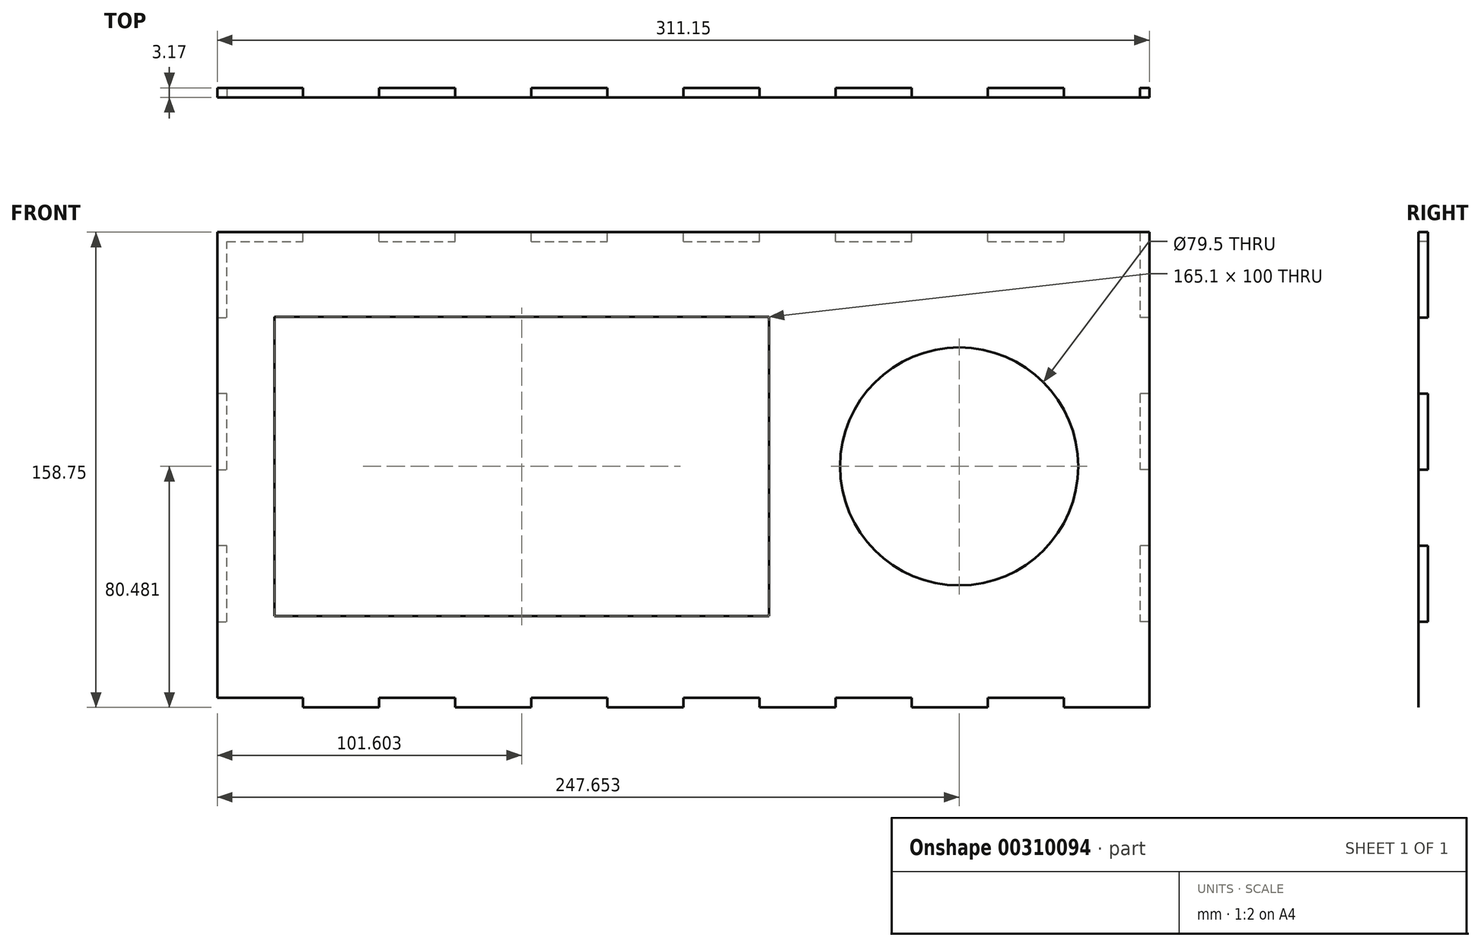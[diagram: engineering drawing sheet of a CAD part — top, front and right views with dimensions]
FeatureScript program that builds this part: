
annotation { "Feature Type Name" : "Feature", "Feature Type Description" : "" }
export const myFeature = defineFeature(function(context is Context, id is Id, definition is map)
    precondition{}
    {
        {
            var Q0;
            Q0=qCreatedBy(makeId("Front.planeOp"),FACE);
            var sketch = newSketch(context, id + "F0", { "sketchPlane" : qUnion([Q0])});
            skLineSegment(sketch, "E0.MirrorCS", {"start": v(-153.56, -44.26) * mm, "end": v(-153.56, -47.44) * mm});
            skLineSegment(sketch, "E1.MirrorCS", {"start": v(-128.16, -44.26) * mm, "end": v(-128.16, -47.44) * mm});
            skLineSegment(sketch, "E2.MirrorCS", {"start": v(-102.76, -44.26) * mm, "end": v(-102.76, -47.44) * mm});
            skLineSegment(sketch, "E3.MirrorCS", {"start": v(-77.36, -44.26) * mm, "end": v(-77.36, -47.44) * mm});
            skLineSegment(sketch, "E4.MirrorCS", {"start": v(-51.96, -44.26) * mm, "end": v(-51.96, -47.44) * mm});
            skLineSegment(sketch, "E5.MirrorCS", {"start": v(-1.16, -44.26) * mm, "end": v(-1.16, -47.44) * mm});
            skLineSegment(sketch, "E6.MirrorCS", {"start": v(-26.56, -44.26) * mm, "end": v(-26.56, -47.44) * mm});
            skLineSegment(sketch, "E7.MirrorCS", {"start": v(49.64, -44.26) * mm, "end": v(49.64, -47.44) * mm});
            skLineSegment(sketch, "E8.MirrorCS", {"start": v(24.24, -44.26) * mm, "end": v(24.24, -47.44) * mm});
            skLineSegment(sketch, "E9.MirrorCS", {"start": v(75.04, -44.26) * mm, "end": v(75.04, -47.44) * mm});
            skLineSegment(sketch, "E10", {"start": v(-178.96, -44.26) * mm, "end": v(-153.56, -44.26) * mm});
            skLineSegment(sketch, "E11", {"start": v(-128.16, -44.26) * mm, "end": v(-102.76, -44.26) * mm});
            skLineSegment(sketch, "E12", {"start": v(-102.76, -47.44) * mm, "end": v(-77.36, -47.44) * mm});
            skLineSegment(sketch, "E13", {"start": v(-77.36, -44.26) * mm, "end": v(-51.96, -44.26) * mm});
            skLineSegment(sketch, "E14", {"start": v(-51.96, -47.44) * mm, "end": v(-26.56, -47.44) * mm});
            skLineSegment(sketch, "E15", {"start": v(-26.56, -44.26) * mm, "end": v(-1.16, -44.26) * mm});
            skLineSegment(sketch, "E16", {"start": v(24.24, -44.26) * mm, "end": v(49.64, -44.26) * mm});
            skLineSegment(sketch, "E17", {"start": v(49.64, -47.44) * mm, "end": v(75.04, -47.44) * mm});
            skLineSegment(sketch, "E18", {"start": v(75.04, -44.26) * mm, "end": v(100.44, -44.26) * mm});
            skLineSegment(sketch, "E19", {"start": v(-182.14, -44.26) * mm, "end": v(-182.14, -18.86) * mm});
            skLineSegment(sketch, "E20", {"start": v(-182.14, -18.86) * mm, "end": v(-178.96, -18.86) * mm});
            skLineSegment(sketch, "E21", {"start": v(-178.96, -18.86) * mm, "end": v(-178.96, 6.54) * mm});
            skLineSegment(sketch, "E22", {"start": v(-178.96, 6.54) * mm, "end": v(-182.14, 6.54) * mm});
            skLineSegment(sketch, "E23", {"start": v(-182.14, 6.54) * mm, "end": v(-182.14, 31.94) * mm});
            skLineSegment(sketch, "E24", {"start": v(-182.14, 31.94) * mm, "end": v(-178.96, 31.94) * mm});
            skLineSegment(sketch, "E25", {"start": v(-178.96, 31.94) * mm, "end": v(-178.96, 57.34) * mm});
            skLineSegment(sketch, "E26", {"start": v(-178.96, 57.34) * mm, "end": v(-182.14, 57.34) * mm});
            skLineSegment(sketch, "E27", {"start": v(-182.14, 57.34) * mm, "end": v(-182.14, 82.74) * mm});
            skLineSegment(sketch, "E28", {"start": v(-182.14, 82.74) * mm, "end": v(-178.96, 82.74) * mm});
            skLineSegment(sketch, "E29", {"start": v(-178.96, 82.74) * mm, "end": v(-178.96, 108.14) * mm});
            skLineSegment(sketch, "E30", {"start": v(-178.96, 108.14) * mm, "end": v(-153.56, 108.14) * mm});
            skLineSegment(sketch, "E31", {"start": v(125.84, 108.14) * mm, "end": v(125.84, 82.74) * mm});
            skLineSegment(sketch, "E32", {"start": v(-1.16, -47.44) * mm, "end": v(24.24, -47.44) * mm});
            skLineSegment(sketch, "E33", {"start": v(-153.56, -47.44) * mm, "end": v(-128.16, -47.44) * mm});
            skLineSegment(sketch, "E34", {"start": v(125.84, -47.44) * mm, "end": v(100.44, -47.44) * mm});
            skLineSegment(sketch, "E35", {"start": v(100.44, -47.44) * mm, "end": v(100.44, -44.26) * mm});
            skLineSegment(sketch, "E36.MirrorCS", {"start": v(-153.56, 111.31) * mm, "end": v(-128.16, 111.31) * mm});
            skLineSegment(sketch, "E37.MirrorCS", {"start": v(-102.76, 111.31) * mm, "end": v(-77.36, 111.31) * mm});
            skLineSegment(sketch, "E38.MirrorCS", {"start": v(-51.96, 111.31) * mm, "end": v(-26.56, 111.31) * mm});
            skLineSegment(sketch, "E39.MirrorCS", {"start": v(-1.16, 111.31) * mm, "end": v(24.24, 111.31) * mm});
            skLineSegment(sketch, "E40.MirrorCS", {"start": v(49.64, 111.31) * mm, "end": v(75.04, 111.31) * mm});
            skLineSegment(sketch, "E41.MirrorCS", {"start": v(125.84, 111.31) * mm, "end": v(100.44, 111.31) * mm});
            skLineSegment(sketch, "E42.MirrorCS", {"start": v(-153.56, 108.14) * mm, "end": v(-153.56, 111.31) * mm});
            skLineSegment(sketch, "E43.MirrorCS", {"start": v(-128.16, 108.14) * mm, "end": v(-128.16, 111.31) * mm});
            skLineSegment(sketch, "E44.MirrorCS", {"start": v(-102.76, 108.14) * mm, "end": v(-102.76, 111.31) * mm});
            skLineSegment(sketch, "E45.MirrorCS", {"start": v(-51.96, 108.14) * mm, "end": v(-51.96, 111.31) * mm});
            skLineSegment(sketch, "E46.MirrorCS", {"start": v(-77.36, 108.14) * mm, "end": v(-77.36, 111.31) * mm});
            skLineSegment(sketch, "E47.MirrorCS", {"start": v(100.44, 111.31) * mm, "end": v(100.44, 108.14) * mm});
            skLineSegment(sketch, "E48.MirrorCS", {"start": v(75.04, 108.14) * mm, "end": v(75.04, 111.31) * mm});
            skLineSegment(sketch, "E49.MirrorCS", {"start": v(49.64, 108.14) * mm, "end": v(49.64, 111.31) * mm});
            skLineSegment(sketch, "E50.MirrorCS", {"start": v(24.24, 108.14) * mm, "end": v(24.24, 111.31) * mm});
            skLineSegment(sketch, "E51.MirrorCS", {"start": v(-26.56, 108.14) * mm, "end": v(-26.56, 111.31) * mm});
            skLineSegment(sketch, "E52.MirrorCS", {"start": v(-1.16, 108.14) * mm, "end": v(-1.16, 111.31) * mm});
            skLineSegment(sketch, "E53.trimOffspring", {"start": v(-128.16, 108.14) * mm, "end": v(-102.76, 108.14) * mm});
            skLineSegment(sketch, "E54.trimOffspring", {"start": v(-77.36, 108.14) * mm, "end": v(-51.96, 108.14) * mm});
            skLineSegment(sketch, "E55.trimOffspring", {"start": v(-26.56, 108.14) * mm, "end": v(-1.16, 108.14) * mm});
            skLineSegment(sketch, "E56.trimOffspring", {"start": v(24.24, 108.14) * mm, "end": v(49.64, 108.14) * mm});
            skLineSegment(sketch, "E57.trimOffspring", {"start": v(75.04, 108.14) * mm, "end": v(100.44, 108.14) * mm});
            skLineSegment(sketch, "E58.MirrorCS", {"start": v(129.01, 57.34) * mm, "end": v(129.01, 82.74) * mm});
            skLineSegment(sketch, "E59.MirrorCS", {"start": v(129.01, 6.54) * mm, "end": v(129.01, 31.94) * mm});
            skLineSegment(sketch, "E60.MirrorCS", {"start": v(129.01, -44.26) * mm, "end": v(129.01, -18.86) * mm});
            skLineSegment(sketch, "E61", {"start": v(129.01, -18.86) * mm, "end": v(125.84, -18.86) * mm});
            skLineSegment(sketch, "E62", {"start": v(129.01, 6.54) * mm, "end": v(125.84, 6.54) * mm});
            skLineSegment(sketch, "E63", {"start": v(129.01, 31.94) * mm, "end": v(125.84, 31.94) * mm});
            skLineSegment(sketch, "E64", {"start": v(125.84, 111.31) * mm, "end": v(125.84, 108.14) * mm});
            skLineSegment(sketch, "E65", {"start": v(129.01, 82.74) * mm, "end": v(125.84, 82.74) * mm});
            skLineSegment(sketch, "E66", {"start": v(129.01, 57.34) * mm, "end": v(125.84, 57.34) * mm});
            skLineSegment(sketch, "E67.trimOffspring", {"start": v(125.84, 57.34) * mm, "end": v(125.84, 31.94) * mm});
            skLineSegment(sketch, "E68.trimOffspring", {"start": v(125.84, 6.54) * mm, "end": v(125.84, -18.86) * mm});
            skLineSegment(sketch, "E69", {"start": v(125.84, -47.44) * mm, "end": v(129.01, -47.44) * mm});
            skLineSegment(sketch, "E70", {"start": v(129.01, -47.44) * mm, "end": v(129.01, -44.26) * mm});
            skPoint(sketch, "E71.end.orphan", {"position": v(125.84, -44.26) * mm});
            skLineSegment(sketch, "E72", {"start": v(-182.14, -44.26) * mm, "end": v(-178.96, -44.26) * mm});
            skPoint(sketch, "E73.end.orphan", {"position": v(-178.96, -47.44) * mm});
            skPoint(sketch, "E74.end.orphan", {"position": v(-182.14, -47.44) * mm});
            skSolve(sketch);
        }
        {
            var Q0;
            Q0=makeQuery(id+"F0.imprint","IMPRINT",FACE,{"disambiguationData":[TD([[makeQuery(id+"F0.imprint","IMPRINT",EDGE,{"derivedFrom":sQuery(id+"F0.wireOp",EDGE,"E0.MirrorCS")}),1.0]])]});
            var Q1;
            Q1=makeQuery(id+"F0.imprint","IMPRINT",FACE,{"disambiguationData":[TD([[makeQuery(id+"F0.imprint","IMPRINT",EDGE,{"derivedFrom":sQuery(id+"F0.wireOp",EDGE,"E5.MirrorCS")}),1.0]])]});
            extrude(context, id + "F1", {"entities" : qUnion([Q0, Q1]), "depth" : 1 / 203.2 * mm});
        }
        {
            var Q0;
            Q0=makeQuery(id+"F1.opExtrude","CAP_FACE",FACE,{"disambiguationData":[OSD([sQuery(id+"F0.wireOp",EDGE,"E0.MirrorCS"),sQuery(id+"F0.wireOp",EDGE,"E1.MirrorCS"),sQuery(id+"F0.wireOp",EDGE,"E2.MirrorCS"),sQuery(id+"F0.wireOp",EDGE,"E3.MirrorCS"),sQuery(id+"F0.wireOp",EDGE,"E4.MirrorCS"),sQuery(id+"F0.wireOp",EDGE,"E5.MirrorCS"),sQuery(id+"F0.wireOp",EDGE,"E6.MirrorCS"),sQuery(id+"F0.wireOp",EDGE,"E7.MirrorCS"),sQuery(id+"F0.wireOp",EDGE,"E8.MirrorCS"),sQuery(id+"F0.wireOp",EDGE,"E9.MirrorCS"),sQuery(id+"F0.wireOp",EDGE,"E10"),sQuery(id+"F0.wireOp",EDGE,"E11"),sQuery(id+"F0.wireOp",EDGE,"E12"),sQuery(id+"F0.wireOp",EDGE,"E13"),sQuery(id+"F0.wireOp",EDGE,"E14"),sQuery(id+"F0.wireOp",EDGE,"E15"),sQuery(id+"F0.wireOp",EDGE,"E16"),sQuery(id+"F0.wireOp",EDGE,"E17"),sQuery(id+"F0.wireOp",EDGE,"E18"),sQuery(id+"F0.wireOp",EDGE,"E19"),sQuery(id+"F0.wireOp",EDGE,"E20"),sQuery(id+"F0.wireOp",EDGE,"E21"),sQuery(id+"F0.wireOp",EDGE,"E22"),sQuery(id+"F0.wireOp",EDGE,"E23"),sQuery(id+"F0.wireOp",EDGE,"E24"),sQuery(id+"F0.wireOp",EDGE,"E25"),sQuery(id+"F0.wireOp",EDGE,"E26"),sQuery(id+"F0.wireOp",EDGE,"E27"),sQuery(id+"F0.wireOp",EDGE,"E28"),sQuery(id+"F0.wireOp",EDGE,"E29"),sQuery(id+"F0.wireOp",EDGE,"E30"),sQuery(id+"F0.wireOp",EDGE,"E31"),sQuery(id+"F0.wireOp",EDGE,"E32"),sQuery(id+"F0.wireOp",EDGE,"E33"),sQuery(id+"F0.wireOp",EDGE,"E34"),sQuery(id+"F0.wireOp",EDGE,"E35"),sQuery(id+"F0.wireOp",EDGE,"E36.MirrorCS"),sQuery(id+"F0.wireOp",EDGE,"E37.MirrorCS"),sQuery(id+"F0.wireOp",EDGE,"E38.MirrorCS"),sQuery(id+"F0.wireOp",EDGE,"E39.MirrorCS"),sQuery(id+"F0.wireOp",EDGE,"E40.MirrorCS"),sQuery(id+"F0.wireOp",EDGE,"E41.MirrorCS"),sQuery(id+"F0.wireOp",EDGE,"E42.MirrorCS"),sQuery(id+"F0.wireOp",EDGE,"E43.MirrorCS"),sQuery(id+"F0.wireOp",EDGE,"E44.MirrorCS"),sQuery(id+"F0.wireOp",EDGE,"E46.MirrorCS"),sQuery(id+"F0.wireOp",EDGE,"E47.MirrorCS"),sQuery(id+"F0.wireOp",EDGE,"E48.MirrorCS"),sQuery(id+"F0.wireOp",EDGE,"E49.MirrorCS"),sQuery(id+"F0.wireOp",EDGE,"E50.MirrorCS"),sQuery(id+"F0.wireOp",EDGE,"E45.MirrorCS"),sQuery(id+"F0.wireOp",EDGE,"E51.MirrorCS"),sQuery(id+"F0.wireOp",EDGE,"E52.MirrorCS"),sQuery(id+"F0.wireOp",EDGE,"E53.trimOffspring"),sQuery(id+"F0.wireOp",EDGE,"E54.trimOffspring"),sQuery(id+"F0.wireOp",EDGE,"E55.trimOffspring"),sQuery(id+"F0.wireOp",EDGE,"E56.trimOffspring"),sQuery(id+"F0.wireOp",EDGE,"E57.trimOffspring"),sQuery(id+"F0.wireOp",EDGE,"E58.MirrorCS"),sQuery(id+"F0.wireOp",EDGE,"E59.MirrorCS"),sQuery(id+"F0.wireOp",EDGE,"E60.MirrorCS"),sQuery(id+"F0.wireOp",EDGE,"E61"),sQuery(id+"F0.wireOp",EDGE,"E62"),sQuery(id+"F0.wireOp",EDGE,"E63"),sQuery(id+"F0.wireOp",EDGE,"E64"),sQuery(id+"F0.wireOp",EDGE,"E65"),sQuery(id+"F0.wireOp",EDGE,"E66"),sQuery(id+"F0.wireOp",EDGE,"E67.trimOffspring"),sQuery(id+"F0.wireOp",EDGE,"E68.trimOffspring"),sQuery(id+"F0.wireOp",EDGE,"E69"),sQuery(id+"F0.wireOp",EDGE,"E70"),sQuery(id+"F0.wireOp",EDGE,"E74"),sQuery(id+"F0.wireOp",EDGE,"E73"),sQuery(id+"F0.wireOp",EDGE,"YqXnORVU-T2M5-09My-Jtlm-RCLeSNGwjOX8")])],"isStart":false});
            var sketch = newSketch(context, id + "F2", { "sketchPlane" : qUnion([Q0])});
            skLineSegment(sketch, "E75.bottom", {"start": v(-163.09, 83.04) * mm, "end": v(2.01, 83.04) * mm});
            skLineSegment(sketch, "E75.top", {"start": v(-163.09, -16.96) * mm, "end": v(2.01, -16.96) * mm});
            skLineSegment(sketch, "E75.left", {"start": v(-163.09, 83.04) * mm, "end": v(-163.09, -16.96) * mm});
            skLineSegment(sketch, "E75.right", {"start": v(2.01, 83.04) * mm, "end": v(2.01, -16.96) * mm});
            skCircle(sketch, "E76", {"center": v(65.51, 33.04) * mm, "radius": 39.75 * mm});
            skPoint(sketch, "E76.centerSnap0", {"position": v(2.01, 33.04) * mm});
            skSolve(sketch);
        }
        {
            var Q0;
            Q0=makeQuery(id+"F2.imprint","IMPRINT",FACE,{"disambiguationData":[TD([[makeQuery(id+"F2.imprint","IMPRINT",EDGE,{"derivedFrom":sQuery(id+"F2.wireOp",EDGE,"E75.bottom")}),-1.0]])]});
            var Q1;
            Q1=makeQuery(id+"F2.imprint","IMPRINT",FACE,{"disambiguationData":[TD([[makeQuery(id+"F2.imprint","IMPRINT",EDGE,{"derivedFrom":sQuery(id+"F2.wireOp",EDGE,"E76")}),1.0]])]});
            extrude(context, id + "F3", {"entities" : qUnion([Q0, Q1]), "operationType" : NewBodyOperationType.REMOVE, "oppositeDirection" : true, "depth" : 25.4 * mm});
        }
        {
            var Q0;
            Q0=makeQuery(id+"F1.opExtrude","CAP_FACE",FACE,{"disambiguationData":[OSD([sQuery(id+"F0.wireOp",EDGE,"E0.MirrorCS"),sQuery(id+"F0.wireOp",EDGE,"E1.MirrorCS"),sQuery(id+"F0.wireOp",EDGE,"E2.MirrorCS"),sQuery(id+"F0.wireOp",EDGE,"E3.MirrorCS"),sQuery(id+"F0.wireOp",EDGE,"E4.MirrorCS"),sQuery(id+"F0.wireOp",EDGE,"E5.MirrorCS"),sQuery(id+"F0.wireOp",EDGE,"E6.MirrorCS"),sQuery(id+"F0.wireOp",EDGE,"E7.MirrorCS"),sQuery(id+"F0.wireOp",EDGE,"E8.MirrorCS"),sQuery(id+"F0.wireOp",EDGE,"E9.MirrorCS"),sQuery(id+"F0.wireOp",EDGE,"E10"),sQuery(id+"F0.wireOp",EDGE,"E11"),sQuery(id+"F0.wireOp",EDGE,"E12"),sQuery(id+"F0.wireOp",EDGE,"E13"),sQuery(id+"F0.wireOp",EDGE,"E14"),sQuery(id+"F0.wireOp",EDGE,"E15"),sQuery(id+"F0.wireOp",EDGE,"E16"),sQuery(id+"F0.wireOp",EDGE,"E17"),sQuery(id+"F0.wireOp",EDGE,"E18"),sQuery(id+"F0.wireOp",EDGE,"E19"),sQuery(id+"F0.wireOp",EDGE,"E20"),sQuery(id+"F0.wireOp",EDGE,"E21"),sQuery(id+"F0.wireOp",EDGE,"E22"),sQuery(id+"F0.wireOp",EDGE,"E23"),sQuery(id+"F0.wireOp",EDGE,"E24"),sQuery(id+"F0.wireOp",EDGE,"E25"),sQuery(id+"F0.wireOp",EDGE,"E26"),sQuery(id+"F0.wireOp",EDGE,"E27"),sQuery(id+"F0.wireOp",EDGE,"E28"),sQuery(id+"F0.wireOp",EDGE,"E29"),sQuery(id+"F0.wireOp",EDGE,"E30"),sQuery(id+"F0.wireOp",EDGE,"E31"),sQuery(id+"F0.wireOp",EDGE,"E32"),sQuery(id+"F0.wireOp",EDGE,"E33"),sQuery(id+"F0.wireOp",EDGE,"E34"),sQuery(id+"F0.wireOp",EDGE,"E35"),sQuery(id+"F0.wireOp",EDGE,"E36.MirrorCS"),sQuery(id+"F0.wireOp",EDGE,"E37.MirrorCS"),sQuery(id+"F0.wireOp",EDGE,"E38.MirrorCS"),sQuery(id+"F0.wireOp",EDGE,"E39.MirrorCS"),sQuery(id+"F0.wireOp",EDGE,"E40.MirrorCS"),sQuery(id+"F0.wireOp",EDGE,"E41.MirrorCS"),sQuery(id+"F0.wireOp",EDGE,"E42.MirrorCS"),sQuery(id+"F0.wireOp",EDGE,"E43.MirrorCS"),sQuery(id+"F0.wireOp",EDGE,"E44.MirrorCS"),sQuery(id+"F0.wireOp",EDGE,"E46.MirrorCS"),sQuery(id+"F0.wireOp",EDGE,"E47.MirrorCS"),sQuery(id+"F0.wireOp",EDGE,"E48.MirrorCS"),sQuery(id+"F0.wireOp",EDGE,"E49.MirrorCS"),sQuery(id+"F0.wireOp",EDGE,"E50.MirrorCS"),sQuery(id+"F0.wireOp",EDGE,"E45.MirrorCS"),sQuery(id+"F0.wireOp",EDGE,"E51.MirrorCS"),sQuery(id+"F0.wireOp",EDGE,"E52.MirrorCS"),sQuery(id+"F0.wireOp",EDGE,"E53.trimOffspring"),sQuery(id+"F0.wireOp",EDGE,"E54.trimOffspring"),sQuery(id+"F0.wireOp",EDGE,"E55.trimOffspring"),sQuery(id+"F0.wireOp",EDGE,"E56.trimOffspring"),sQuery(id+"F0.wireOp",EDGE,"E57.trimOffspring"),sQuery(id+"F0.wireOp",EDGE,"E58.MirrorCS"),sQuery(id+"F0.wireOp",EDGE,"E59.MirrorCS"),sQuery(id+"F0.wireOp",EDGE,"E60.MirrorCS"),sQuery(id+"F0.wireOp",EDGE,"E61"),sQuery(id+"F0.wireOp",EDGE,"E62"),sQuery(id+"F0.wireOp",EDGE,"E63"),sQuery(id+"F0.wireOp",EDGE,"E64"),sQuery(id+"F0.wireOp",EDGE,"E65"),sQuery(id+"F0.wireOp",EDGE,"E66"),sQuery(id+"F0.wireOp",EDGE,"E67.trimOffspring"),sQuery(id+"F0.wireOp",EDGE,"E68.trimOffspring"),sQuery(id+"F0.wireOp",EDGE,"E69"),sQuery(id+"F0.wireOp",EDGE,"E70"),sQuery(id+"F0.wireOp",EDGE,"E72")])],"isStart":false});
            var sketch = newSketch(context, id + "F4", { "sketchPlane" : qUnion([Q0])});
            skLineSegment(sketch, "E77.bottom", {"start": v(129.01, -47.44) * mm, "end": v(-182.14, -47.44) * mm});
            skLineSegment(sketch, "E77.top", {"start": v(129.01, 111.31) * mm, "end": v(-182.14, 111.31) * mm});
            skLineSegment(sketch, "E77.left", {"start": v(129.01, -47.44) * mm, "end": v(129.01, 111.31) * mm});
            skLineSegment(sketch, "E77.right", {"start": v(-182.14, -47.44) * mm, "end": v(-182.14, 111.31) * mm});
            skSolve(sketch);
        }
        {
            var Q0;
            {var subQ0=makeQuery(id+"F1.opExtrude","CAP_EDGE",EDGE,{"disambiguationData":[OSD([sQuery(id+"F0.wireOp",EDGE,"E28")])],"isStart":false});Q0=makeQuery(id+"F4.imprint","IMPRINT",FACE,{"disambiguationData":[TD([[makeQuery(id+"F4.imprint","IMPRINT",EDGE,{"derivedFrom":subQ0}),1.0]])]});}
            var Q1;
            {var subQ1=makeQuery(id+"F1.opExtrude","CAP_EDGE",EDGE,{"disambiguationData":[OSD([sQuery(id+"F0.wireOp",EDGE,"E24")])],"isStart":false});Q1=makeQuery(id+"F4.imprint","IMPRINT",FACE,{"disambiguationData":[TD([[makeQuery(id+"F4.imprint","IMPRINT",EDGE,{"derivedFrom":subQ1}),1.0]])]});}
            var Q2;
            {var subQ1=makeQuery(id+"F1.opExtrude","CAP_EDGE",EDGE,{"disambiguationData":[OSD([sQuery(id+"F0.wireOp",EDGE,"E20")])],"isStart":false});Q2=makeQuery(id+"F4.imprint","IMPRINT",FACE,{"disambiguationData":[TD([[makeQuery(id+"F4.imprint","IMPRINT",EDGE,{"derivedFrom":subQ1}),1.0]])]});}
            var Q3;
            {var subQ2=makeQuery(id+"F1.opExtrude","CAP_EDGE",EDGE,{"disambiguationData":[OSD([sQuery(id+"F0.wireOp",EDGE,"E61")])],"isStart":false});Q3=makeQuery(id+"F4.imprint","IMPRINT",FACE,{"disambiguationData":[TD([[makeQuery(id+"F4.imprint","IMPRINT",EDGE,{"derivedFrom":subQ2}),-1.0]])]});}
            var Q4;
            {var subQ2=makeQuery(id+"F1.opExtrude","CAP_EDGE",EDGE,{"disambiguationData":[OSD([sQuery(id+"F0.wireOp",EDGE,"E63")])],"isStart":false});Q4=makeQuery(id+"F4.imprint","IMPRINT",FACE,{"disambiguationData":[TD([[makeQuery(id+"F4.imprint","IMPRINT",EDGE,{"derivedFrom":subQ2}),-1.0]])]});}
            var Q5;
            {var subQ4=makeQuery(id+"F1.opExtrude","CAP_EDGE",EDGE,{"disambiguationData":[OSD([sQuery(id+"F0.wireOp",EDGE,"E65")])],"isStart":false});Q5=makeQuery(id+"F4.imprint","IMPRINT",FACE,{"disambiguationData":[TD([[makeQuery(id+"F4.imprint","IMPRINT",EDGE,{"derivedFrom":subQ4}),-1.0]])]});}
            var Q6;
            {var subQ2=makeQuery(id+"F1.opExtrude","CAP_EDGE",EDGE,{"disambiguationData":[OSD([sQuery(id+"F0.wireOp",EDGE,"E47.MirrorCS")])],"isStart":false});Q6=makeQuery(id+"F4.imprint","IMPRINT",FACE,{"disambiguationData":[TD([[makeQuery(id+"F4.imprint","IMPRINT",EDGE,{"derivedFrom":subQ2}),-1.0]])]});}
            var Q7;
            {var subQ2=makeQuery(id+"F1.opExtrude","CAP_EDGE",EDGE,{"disambiguationData":[OSD([sQuery(id+"F0.wireOp",EDGE,"E49.MirrorCS")])],"isStart":false});Q7=makeQuery(id+"F4.imprint","IMPRINT",FACE,{"disambiguationData":[TD([[makeQuery(id+"F4.imprint","IMPRINT",EDGE,{"derivedFrom":subQ2}),1.0]])]});}
            var Q8;
            {var subQ1=makeQuery(id+"F1.opExtrude","CAP_EDGE",EDGE,{"disambiguationData":[OSD([sQuery(id+"F0.wireOp",EDGE,"E51.MirrorCS")])],"isStart":false});Q8=makeQuery(id+"F4.imprint","IMPRINT",FACE,{"disambiguationData":[TD([[makeQuery(id+"F4.imprint","IMPRINT",EDGE,{"derivedFrom":subQ1}),-1.0]])]});}
            var Q9;
            {var subQ1=makeQuery(id+"F1.opExtrude","CAP_EDGE",EDGE,{"disambiguationData":[OSD([sQuery(id+"F0.wireOp",EDGE,"E46.MirrorCS")])],"isStart":false});Q9=makeQuery(id+"F4.imprint","IMPRINT",FACE,{"disambiguationData":[TD([[makeQuery(id+"F4.imprint","IMPRINT",EDGE,{"derivedFrom":subQ1}),-1.0]])]});}
            var Q10;
            {var subQ1=makeQuery(id+"F1.opExtrude","CAP_EDGE",EDGE,{"disambiguationData":[OSD([sQuery(id+"F0.wireOp",EDGE,"E43.MirrorCS")])],"isStart":false});Q10=makeQuery(id+"F4.imprint","IMPRINT",FACE,{"disambiguationData":[TD([[makeQuery(id+"F4.imprint","IMPRINT",EDGE,{"derivedFrom":subQ1}),-1.0]])]});}
            extrude(context, id + "F5", {"entities" : qUnion([Q0, Q1, Q2, Q3, Q4, Q5, Q6, Q7, Q8, Q9, Q10]), "operationType" : NewBodyOperationType.ADD, "oppositeDirection" : true, "depth" : 3.17 * mm});
        }
    });
